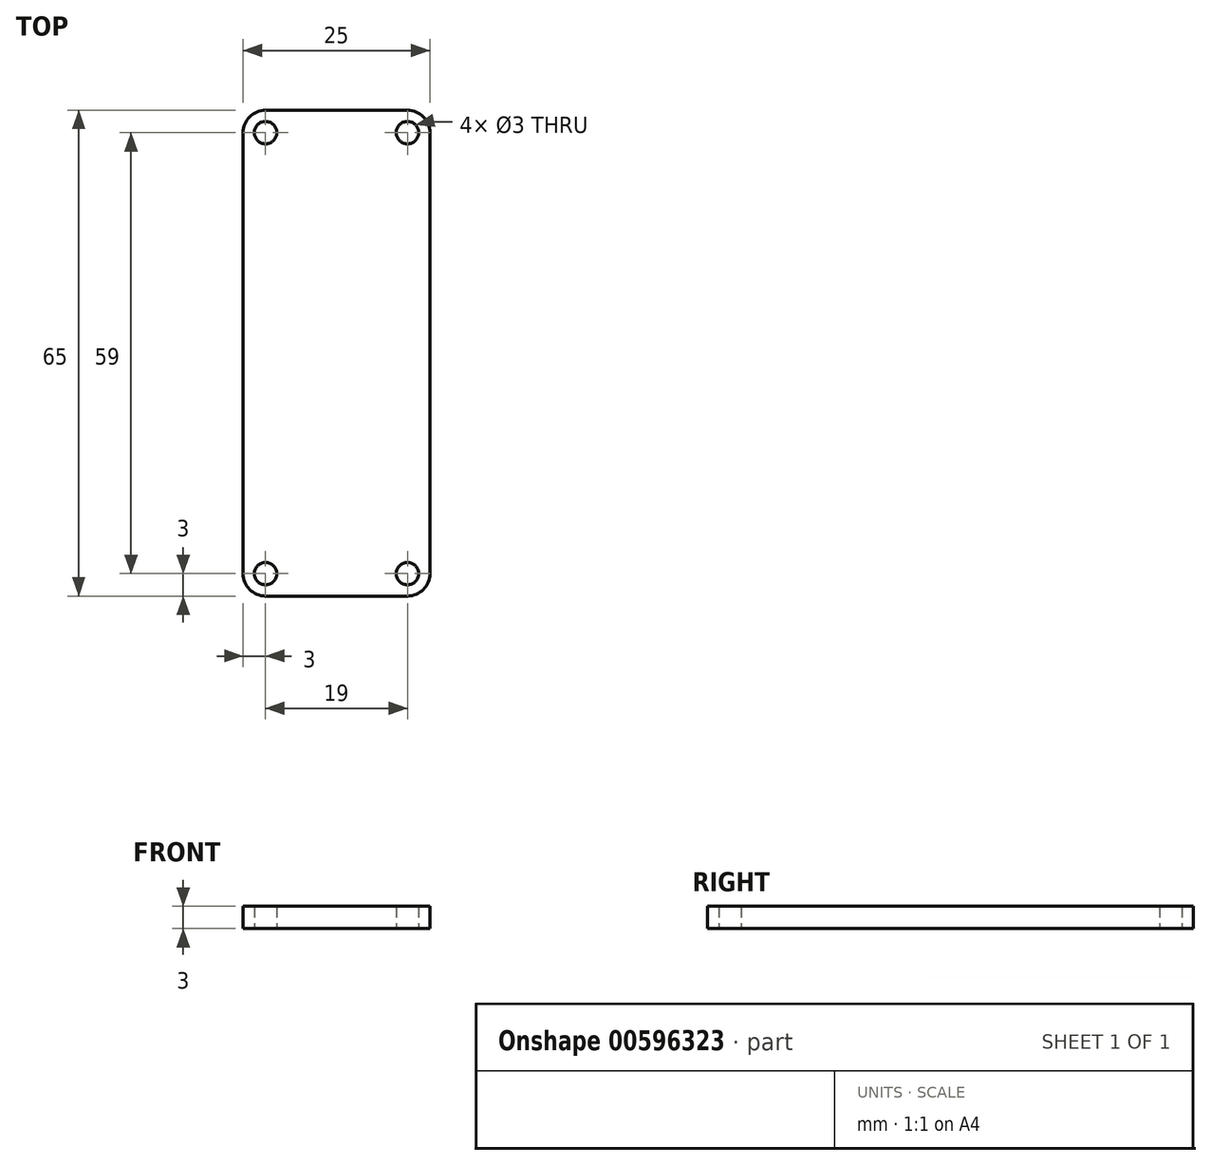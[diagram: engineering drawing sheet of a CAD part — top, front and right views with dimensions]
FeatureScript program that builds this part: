
annotation { "Feature Type Name" : "Feature", "Feature Type Description" : "" }
export const myFeature = defineFeature(function(context is Context, id is Id, definition is map)
    precondition{}
    {
        {
            var Q0;
            Q0=qCreatedBy(makeId("Top.planeOp"),FACE);
            var sketch = newSketch(context, id + "F0", { "sketchPlane" : qUnion([Q0])});
            skLineSegment(sketch, "E0.bottom", {"start": v(9.5, 32.5) * mm, "end": v(-9.5, 32.5) * mm});
            skLineSegment(sketch, "E0.top", {"start": v(9.5, -32.5) * mm, "end": v(-9.5, -32.5) * mm});
            skLineSegment(sketch, "E0.left", {"start": v(12.5, 29.5) * mm, "end": v(12.5, -29.5) * mm});
            skLineSegment(sketch, "E0.right", {"start": v(-12.5, 29.5) * mm, "end": v(-12.5, -29.5) * mm});
            skPoint(sketch, "E0.middle", {"position": v(0, 0) * mm});
            skPoint(sketch, "E1.visualSharp", {"position": v(-12.5, 32.5) * mm});
            skArc(sketch, "E1.filletArc", {"start": v(-9.5, 32.5) * mm, "mid": v(-11.62, 31.62) * mm, "end": v(-12.5, 29.5) * mm});
            skPoint(sketch, "E2.visualSharp", {"position": v(12.5, 32.5) * mm});
            skArc(sketch, "E2.filletArc", {"start": v(12.5, 29.5) * mm, "mid": v(11.62, 31.62) * mm, "end": v(9.5, 32.5) * mm});
            skPoint(sketch, "E3.visualSharp", {"position": v(12.5, -32.5) * mm});
            skArc(sketch, "E3.filletArc", {"start": v(9.5, -32.5) * mm, "mid": v(11.62, -31.62) * mm, "end": v(12.5, -29.5) * mm});
            skPoint(sketch, "E4.visualSharp", {"position": v(-12.5, -32.5) * mm});
            skArc(sketch, "E4.filletArc", {"start": v(-12.5, -29.5) * mm, "mid": v(-11.62, -31.62) * mm, "end": v(-9.5, -32.5) * mm});
            skCircle(sketch, "E5", {"center": v(-9.5, 29.5) * mm, "radius": 1.5 * mm});
            skCircle(sketch, "E6", {"center": v(9.5, 29.5) * mm, "radius": 1.5 * mm});
            skCircle(sketch, "E7", {"center": v(-9.5, -29.5) * mm, "radius": 1.5 * mm});
            skCircle(sketch, "E8", {"center": v(9.5, -29.5) * mm, "radius": 1.5 * mm});
            skSolve(sketch);
        }
        {
            var Q0;
            Q0 = qSketchRegion(id + "F0", true);
            extrude(context, id + "F1", {"entities" : qUnion([Q0]), "depth" : 3 * mm, "offsetDistance" : 25 * mm});
        }
    });
